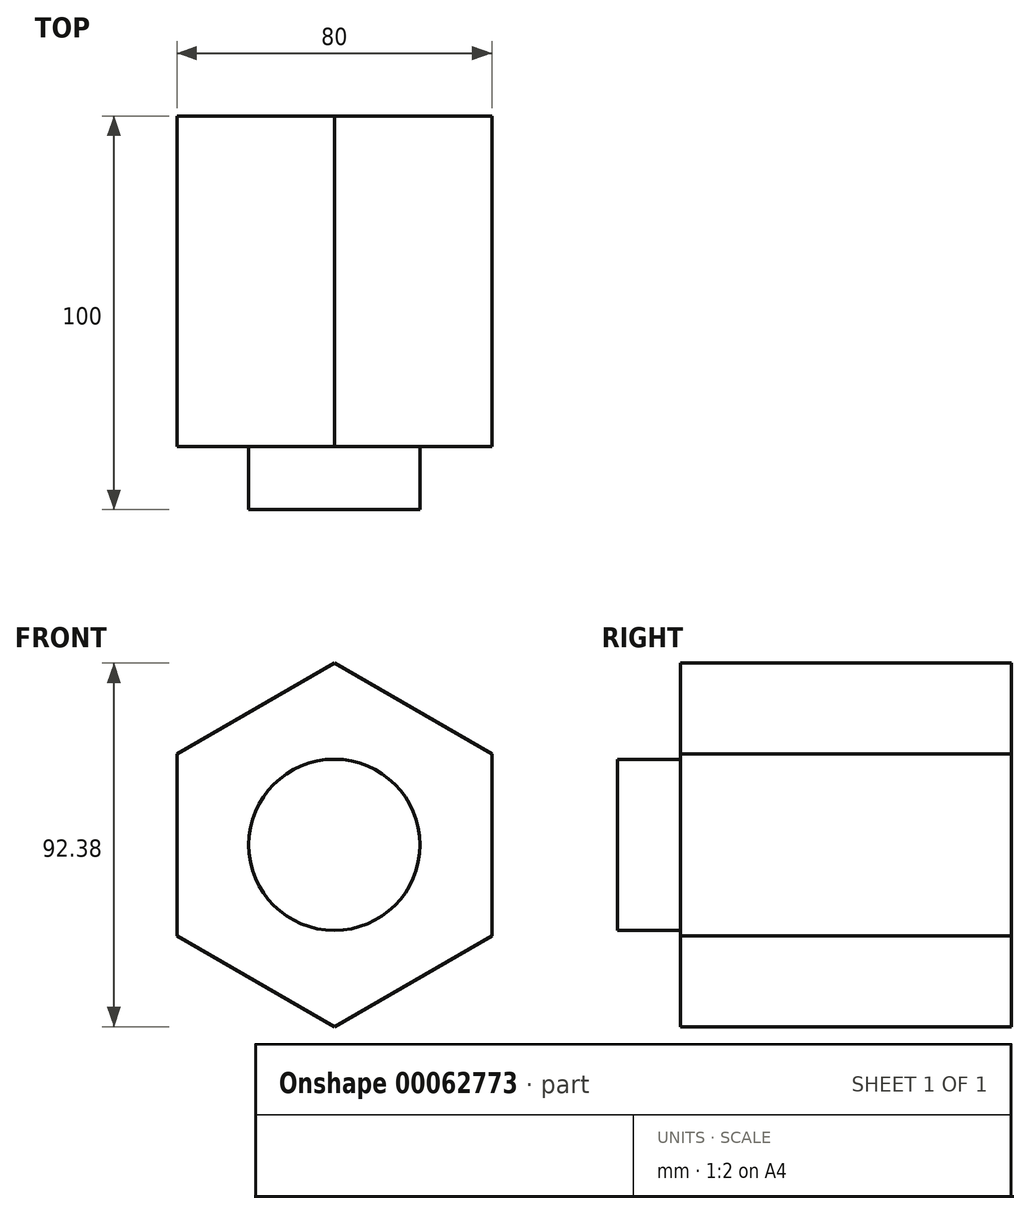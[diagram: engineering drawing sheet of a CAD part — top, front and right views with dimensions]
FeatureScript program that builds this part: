
annotation { "Feature Type Name" : "Feature", "Feature Type Description" : "" }
export const myFeature = defineFeature(function(context is Context, id is Id, definition is map)
    precondition{}
    {
        {
            var Q0;
            Q0=qCreatedBy(makeId("Front.planeOp"),FACE);
            var sketch = newSketch(context, id + "F0", { "sketchPlane" : qUnion([Q0])});
            skCircle(sketch, "E0", {"center": v(0, 0) * mm, "radius": 21.75 * mm});
            skSolve(sketch);
        }
        {
            var Q0;
            Q0=qSketchRegion(id+"F0",true);
            extrude(context, id + "F1", {"entities" : qUnion([Q0]), "oppositeDirection" : true, "depth" : 16 * mm});
        }
        {
            var Q0;
            Q0=makeQuery(id+"F1.opExtrude","CAP_FACE",FACE,{"disambiguationData":[OSD([sQuery(id+"F0.wireOp",EDGE,"E0")])],"isStart":false});
            var sketch = newSketch(context, id + "F2", { "sketchPlane" : qUnion([Q0])});
            skCircle(sketch, "E1.cCircle", {"center": v(0, 0) * mm, "radius": 40 * mm, "construction": true});
            skLineSegment(sketch, "E1.0", {"start": v(40, 23.1) * mm, "end": v(40, -23.1) * mm});
            skLineSegment(sketch, "E1.1", {"start": v(40, -23.1) * mm, "end": v(0, -46.19) * mm});
            skLineSegment(sketch, "E1.2", {"start": v(0, -46.19) * mm, "end": v(-40, -23.1) * mm});
            skLineSegment(sketch, "E1.3", {"start": v(-40, -23.1) * mm, "end": v(-40, 23.1) * mm});
            skLineSegment(sketch, "E1.4", {"start": v(-40, 23.1) * mm, "end": v(0, 46.19) * mm});
            skLineSegment(sketch, "E1.5", {"start": v(0, 46.19) * mm, "end": v(40, 23.1) * mm});
            skPoint(sketch, "E1.0.midPoint", {"position": v(40, 0) * mm});
            skSolve(sketch);
        }
        {
            var Q0;
            Q0=qSketchRegion(id+"F2",true);
            extrude(context, id + "F3", {"entities" : qUnion([Q0]), "operationType" : NewBodyOperationType.ADD, "depth" : (100 - 16) * mm});
        }
    });
